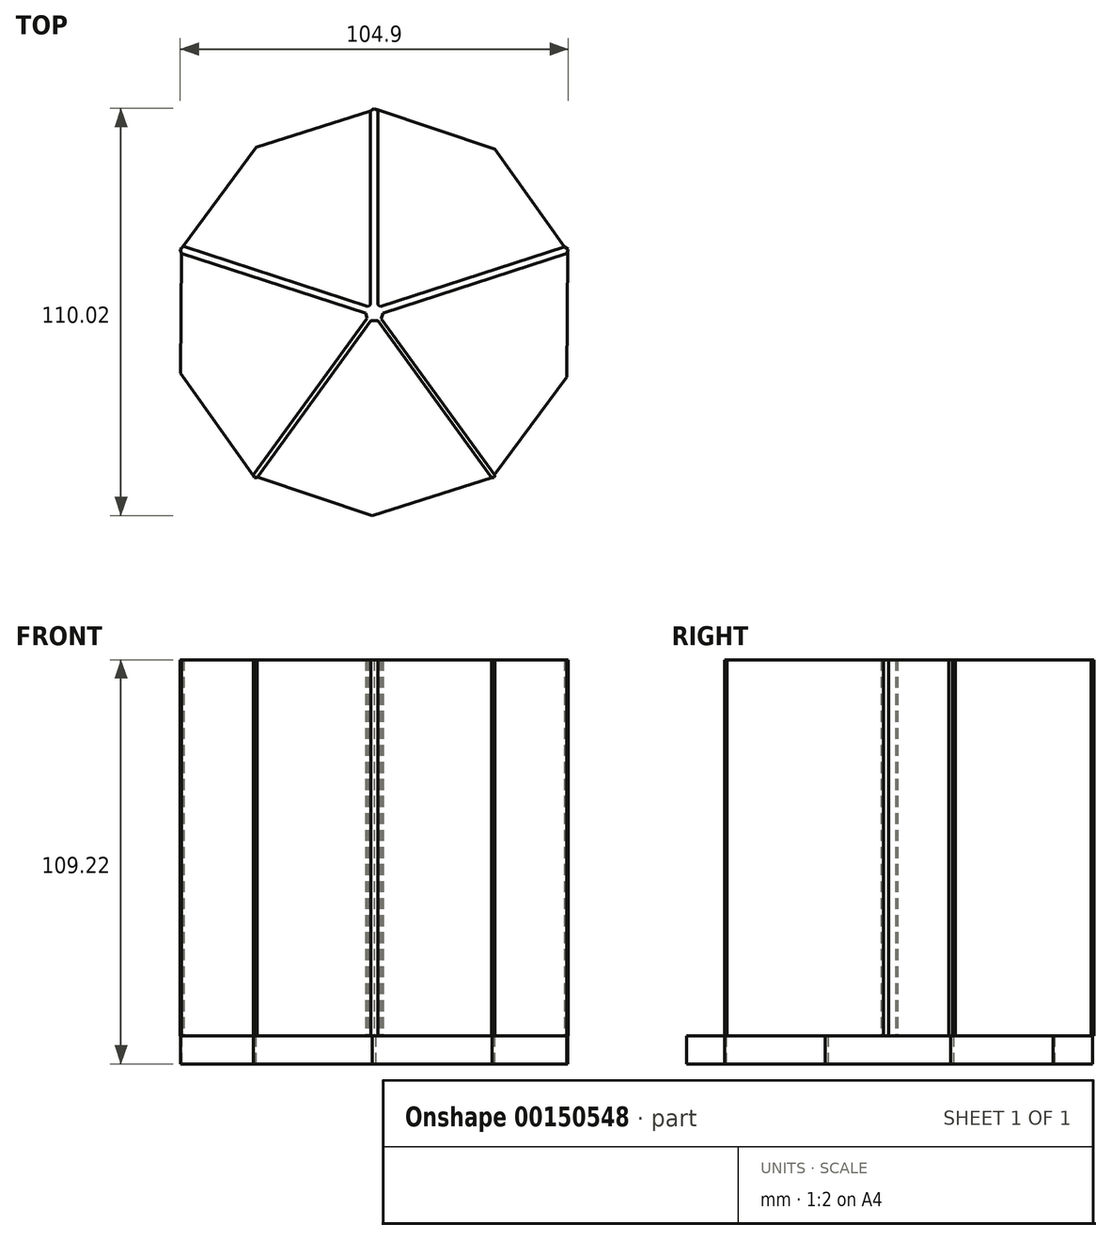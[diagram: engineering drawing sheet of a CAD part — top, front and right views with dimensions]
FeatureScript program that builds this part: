
annotation { "Feature Type Name" : "Feature", "Feature Type Description" : "" }
export const myFeature = defineFeature(function(context is Context, id is Id, definition is map)
    precondition{}
    {
        {
            var Q0;
            Q0=qCreatedBy(makeId("Top.planeOp"),FACE);
            var sketch = newSketch(context, id + "F0", { "sketchPlane" : qUnion([Q0])});
            skLineSegment(sketch, "E0.0", {"start": v(0.03, 55.15) * mm, "end": v(52.46, 17.02) * mm});
            skLineSegment(sketch, "E0.1", {"start": v(52.46, 17.02) * mm, "end": v(32.4, -44.63) * mm});
            skLineSegment(sketch, "E0.2", {"start": v(32.4, -44.63) * mm, "end": v(-32.44, -44.6) * mm});
            skLineSegment(sketch, "E0.3", {"start": v(-32.44, -44.6) * mm, "end": v(-52.44, 17.07) * mm});
            skLineSegment(sketch, "E0.4", {"start": v(-52.44, 17.07) * mm, "end": v(0.03, 55.15) * mm});
            skPoint(sketch, "E0.0.midPoint", {"position": v(26.24, 36.08) * mm});
            skLineSegment(sketch, "E1.0", {"start": v(0, 2.82) * mm, "end": v(2.68, 0.87) * mm});
            skLineSegment(sketch, "E1.1", {"start": v(2.68, 0.87) * mm, "end": v(1.65, -2.28) * mm});
            skLineSegment(sketch, "E1.2", {"start": v(1.65, -2.28) * mm, "end": v(-1.66, -2.28) * mm});
            skLineSegment(sketch, "E1.3", {"start": v(-1.66, -2.28) * mm, "end": v(-2.68, 0.88) * mm});
            skLineSegment(sketch, "E1.4", {"start": v(-2.68, 0.88) * mm, "end": v(0, 2.82) * mm});
            skPoint(sketch, "E1.0.midPoint", {"position": v(1.34, 1.84) * mm});
            skLineSegment(sketch, "E2", {"start": v(-51.43, 17.8) * mm, "end": v(-1.67, 1.61) * mm});
            skLineSegment(sketch, "E3", {"start": v(-52.08, 15.95) * mm, "end": v(-2.32, -0.24) * mm});
            skLineSegment(sketch, "E4", {"start": v(-1, 2.1) * mm, "end": v(-0.98, 54.42) * mm});
            skLineSegment(sketch, "E5", {"start": v(1, 2.1) * mm, "end": v(1, 54.44) * mm});
            skLineSegment(sketch, "E6", {"start": v(1.66, 1.61) * mm, "end": v(51.44, 17.76) * mm});
            skLineSegment(sketch, "E7", {"start": v(2.32, -0.24) * mm, "end": v(52.1, 15.91) * mm});
            skLineSegment(sketch, "E8", {"start": v(-1.9, -1.57) * mm, "end": v(-32.67, -43.89) * mm});
            skLineSegment(sketch, "E9", {"start": v(-0.9, -2.28) * mm, "end": v(-31.68, -44.6) * mm});
            skLineSegment(sketch, "E10", {"start": v(0.97, -2.28) * mm, "end": v(31.71, -44.63) * mm});
            skLineSegment(sketch, "E11", {"start": v(32.59, -44.04) * mm, "end": v(1.85, -1.69) * mm});
            skLineSegment(sketch, "E12", {"start": v(-31.68, -44.6) * mm, "end": v(-30.2, -42.55) * mm});
            skLineSegment(sketch, "E13", {"start": v(-32.67, -43.89) * mm, "end": v(-31.18, -41.84) * mm});
            skLineSegment(sketch, "E14", {"start": v(31.71, -44.63) * mm, "end": v(30.22, -42.58) * mm});
            skLineSegment(sketch, "E15", {"start": v(32.59, -44.04) * mm, "end": v(31.09, -41.96) * mm});
            skLineSegment(sketch, "E16", {"start": v(-52.08, 15.95) * mm, "end": v(-49.67, 15.17) * mm});
            skLineSegment(sketch, "E17", {"start": v(-51.43, 17.8) * mm, "end": v(-49.02, 17.02) * mm});
            skLineSegment(sketch, "E18", {"start": v(-0.98, 54.42) * mm, "end": v(-0.98, 51.88) * mm});
            skLineSegment(sketch, "E19", {"start": v(1, 54.44) * mm, "end": v(1, 51.9) * mm});
            skLineSegment(sketch, "E20", {"start": v(51.44, 17.76) * mm, "end": v(49.01, 16.97) * mm});
            skLineSegment(sketch, "E21", {"start": v(52.1, 15.91) * mm, "end": v(49.68, 15.13) * mm});
            skLineSegment(sketch, "E22", {"start": v(31.09, -41.96) * mm, "end": v(49.68, 15.13) * mm});
            skLineSegment(sketch, "E23", {"start": v(49.01, 16.97) * mm, "end": v(1, 51.9) * mm});
            skLineSegment(sketch, "E24", {"start": v(1, 51.9) * mm, "end": v(-0.98, 51.88) * mm});
            skLineSegment(sketch, "E25", {"start": v(-0.98, 51.88) * mm, "end": v(-49.02, 17.02) * mm});
            skLineSegment(sketch, "E26", {"start": v(-49.02, 17.02) * mm, "end": v(-49.67, 15.17) * mm});
            skLineSegment(sketch, "E27", {"start": v(-49.67, 15.17) * mm, "end": v(-31.18, -41.84) * mm});
            skLineSegment(sketch, "E28", {"start": v(-31.18, -41.84) * mm, "end": v(-30.2, -42.55) * mm});
            skLineSegment(sketch, "E29", {"start": v(-30.2, -42.55) * mm, "end": v(30.22, -42.58) * mm});
            skLineSegment(sketch, "E30", {"start": v(30.22, -42.58) * mm, "end": v(31.09, -41.96) * mm});
            skLineSegment(sketch, "E31", {"start": v(49.68, 15.13) * mm, "end": v(49.01, 16.97) * mm});
            skSolve(sketch);
        }
        {
            var Q0;
            {var subQ4=sQuery(id+"F0.wireOp",EDGE,"E4");Q0=makeQuery(id+"F0.imprint","IMPRINT",FACE,{"disambiguationData":[TD([[makeQuery(id+"F0.imprint","IMPRINT",EDGE,{"derivedFrom":subQ4}),-1.0]])]});}
            var Q1;
            {var subQ1=sQuery(id+"F0.wireOp",EDGE,"E20");Q1=makeQuery(id+"F0.imprint","IMPRINT",FACE,{"disambiguationData":[TD([[makeQuery(id+"F0.imprint","IMPRINT",EDGE,{"derivedFrom":subQ1}),1.0]])]});}
            var Q2;
            {var subQ1=sQuery(id+"F0.wireOp",EDGE,"E2");Q2=makeQuery(id+"F0.imprint","IMPRINT",FACE,{"disambiguationData":[TD([[makeQuery(id+"F0.imprint","IMPRINT",EDGE,{"derivedFrom":subQ1}),-1.0]])]});}
            var Q3;
            {var subQ1=sQuery(id+"F0.wireOp",EDGE,"E16");Q3=makeQuery(id+"F0.imprint","IMPRINT",FACE,{"disambiguationData":[TD([[makeQuery(id+"F0.imprint","IMPRINT",EDGE,{"derivedFrom":subQ1}),1.0]])]});}
            var Q4;
            {var subQ1=sQuery(id+"F0.wireOp",EDGE,"E6");Q4=makeQuery(id+"F0.imprint","IMPRINT",FACE,{"disambiguationData":[TD([[makeQuery(id+"F0.imprint","IMPRINT",EDGE,{"derivedFrom":subQ1}),-1.0]])]});}
            var Q5;
            {var subQ7=sQuery(id+"F0.wireOp",EDGE,"E1.4");var subQ8=sQuery(id+"F0.wireOp",EDGE,"E1.0");var subQ9=makeQuery(id+"F0.imprint","INTERSECT",VERTEX,{"derivedFrom":[subQ8,subQ7]});Q5=makeQuery(id+"F0.imprint","IMPRINT",FACE,{"disambiguationData":[TD([[makeQuery(id+"F0.imprint","IMPRINT",EDGE,{"disambiguationData":[TD([[subQ9,-1.0]])],"derivedFrom":subQ8}),-1.0]])]});}
            var Q6;
            {var subQ0=sQuery(id+"F0.wireOp",EDGE,"E17");Q6=makeQuery(id+"F0.imprint","IMPRINT",FACE,{"disambiguationData":[TD([[makeQuery(id+"F0.imprint","IMPRINT",EDGE,{"derivedFrom":subQ0}),1.0]])]});}
            var Q7;
            {var subQ0=sQuery(id+"F0.wireOp",EDGE,"E19");Q7=makeQuery(id+"F0.imprint","IMPRINT",FACE,{"disambiguationData":[TD([[makeQuery(id+"F0.imprint","IMPRINT",EDGE,{"derivedFrom":subQ0}),1.0]])]});}
            var Q8;
            {var subQ0=sQuery(id+"F0.wireOp",EDGE,"E12");Q8=makeQuery(id+"F0.imprint","IMPRINT",FACE,{"disambiguationData":[TD([[makeQuery(id+"F0.imprint","IMPRINT",EDGE,{"derivedFrom":subQ0}),-1.0]])]});}
            var Q9;
            {var subQ1=sQuery(id+"F0.wireOp",EDGE,"E10");Q9=makeQuery(id+"F0.imprint","IMPRINT",FACE,{"disambiguationData":[TD([[makeQuery(id+"F0.imprint","IMPRINT",EDGE,{"derivedFrom":subQ1}),1.0]])]});}
            var Q10;
            {var subQ0=sQuery(id+"F0.wireOp",EDGE,"E15");Q10=makeQuery(id+"F0.imprint","IMPRINT",FACE,{"disambiguationData":[TD([[makeQuery(id+"F0.imprint","IMPRINT",EDGE,{"derivedFrom":subQ0}),-1.0]])]});}
            var Q11;
            {var subQ0=sQuery(id+"F0.wireOp",EDGE,"E13");Q11=makeQuery(id+"F0.imprint","IMPRINT",FACE,{"disambiguationData":[TD([[makeQuery(id+"F0.imprint","IMPRINT",EDGE,{"derivedFrom":subQ0}),1.0]])]});}
            var Q12;
            {var subQ4=sQuery(id+"F0.wireOp",EDGE,"E8");Q12=makeQuery(id+"F0.imprint","IMPRINT",FACE,{"disambiguationData":[TD([[makeQuery(id+"F0.imprint","IMPRINT",EDGE,{"derivedFrom":subQ4}),1.0]])]});}
            var Q13;
            {var subQ1=sQuery(id+"F0.wireOp",EDGE,"E18");Q13=makeQuery(id+"F0.imprint","IMPRINT",FACE,{"disambiguationData":[TD([[makeQuery(id+"F0.imprint","IMPRINT",EDGE,{"derivedFrom":subQ1}),1.0]])]});}
            var Q14;
            {var subQ1=sQuery(id+"F0.wireOp",EDGE,"E12");Q14=makeQuery(id+"F0.imprint","IMPRINT",FACE,{"disambiguationData":[TD([[makeQuery(id+"F0.imprint","IMPRINT",EDGE,{"derivedFrom":subQ1}),1.0]])]});}
            var Q15;
            {var subQ4=sQuery(id+"F0.wireOp",EDGE,"E14");Q15=makeQuery(id+"F0.imprint","IMPRINT",FACE,{"disambiguationData":[TD([[makeQuery(id+"F0.imprint","IMPRINT",EDGE,{"derivedFrom":subQ4}),-1.0]])]});}
            extrude(context, id + "F1", {"entities" : qUnion([Q0, Q1, Q2, Q3, Q4, Q5, Q6, Q7, Q8, Q9, Q10, Q11, Q12, Q13, Q14, Q15]), "depth" : 101.6 * mm});
        }
        {
            var Q0;
            Q0=qCreatedBy(makeId("Top.planeOp"),FACE);
            var sketch = newSketch(context, id + "F2", { "sketchPlane" : qUnion([Q0])});
            skLineSegment(sketch, "E32.0", {"start": v(31.86, -44.68) * mm, "end": v(-0.48, -54.87) * mm});
            skLineSegment(sketch, "E32.1", {"start": v(-0.48, -54.87) * mm, "end": v(-32.64, -44.1) * mm});
            skLineSegment(sketch, "E32.2", {"start": v(-32.64, -44.1) * mm, "end": v(-52.34, -16.5) * mm});
            skLineSegment(sketch, "E32.3", {"start": v(-52.34, -16.5) * mm, "end": v(-52.04, 17.42) * mm});
            skLineSegment(sketch, "E32.4", {"start": v(-52.04, 17.42) * mm, "end": v(-31.86, 44.68) * mm});
            skLineSegment(sketch, "E32.5", {"start": v(-31.86, 44.68) * mm, "end": v(0.48, 54.87) * mm});
            skLineSegment(sketch, "E32.6", {"start": v(0.48, 54.87) * mm, "end": v(32.64, 44.1) * mm});
            skLineSegment(sketch, "E32.7", {"start": v(32.64, 44.1) * mm, "end": v(52.34, 16.5) * mm});
            skLineSegment(sketch, "E32.8", {"start": v(52.34, 16.5) * mm, "end": v(52.04, -17.42) * mm});
            skLineSegment(sketch, "E32.9", {"start": v(52.04, -17.42) * mm, "end": v(31.86, -44.68) * mm});
            skSolve(sketch);
        }
        {
            var Q0;
            Q0=qSketchRegion(id+"F2",true);
            extrude(context, id + "F3", {"entities" : qUnion([Q0]), "operationType" : NewBodyOperationType.ADD, "oppositeDirection" : true, "depth" : 7.62 * mm});
        }
    });
